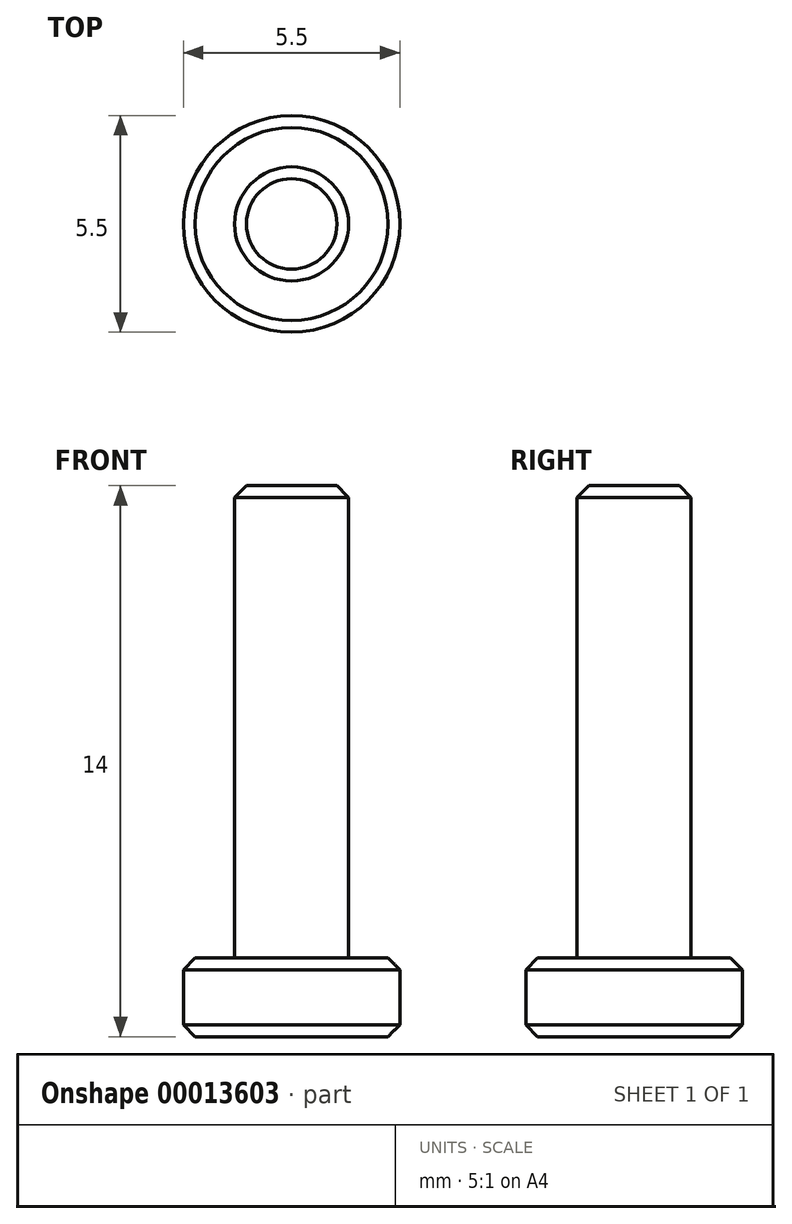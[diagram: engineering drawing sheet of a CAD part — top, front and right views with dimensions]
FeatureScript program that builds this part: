
annotation { "Feature Type Name" : "Feature", "Feature Type Description" : "" }
export const myFeature = defineFeature(function(context is Context, id is Id, definition is map)
    precondition{}
    {
        {
            var Q0;
            Q0=qCreatedBy(makeId("Top.planeOp"),FACE);
            var sketch = newSketch(context, id + "F0", { "sketchPlane" : qUnion([Q0])});
            skCircle(sketch, "E0", {"center": v(0, 0) * mm, "radius": 2.75 * mm});
            skCircle(sketch, "E1", {"center": v(0, 0) * mm, "radius": 1.45 * mm});
            skSolve(sketch);
        }
        {
            var Q0;
            Q0=makeQuery(id+"F0.imprint","IMPRINT",FACE,{"disambiguationData":[TD([[makeQuery(id+"F0.imprint","IMPRINT",EDGE,{"derivedFrom":sQuery(id+"F0.wireOp",EDGE,"E1")}),1.0]])]});
            var Q1;
            Q1=makeQuery(id+"F0.imprint","IMPRINT",FACE,{"disambiguationData":[TD([[makeQuery(id+"F0.imprint","IMPRINT",EDGE,{"derivedFrom":sQuery(id+"F0.wireOp",EDGE,"E0")}),1.0]])]});
            extrude(context, id + "F1", {"entities" : qUnion([Q0, Q1]), "oppositeDirection" : true, "depth" : 2 * mm});
        }
        {
            var Q0;
            Q0=makeQuery(id+"F0.imprint","IMPRINT",FACE,{"disambiguationData":[TD([[makeQuery(id+"F0.imprint","IMPRINT",EDGE,{"derivedFrom":sQuery(id+"F0.wireOp",EDGE,"E1")}),1.0]])]});
            extrude(context, id + "F2", {"entities" : qUnion([Q0]), "operationType" : NewBodyOperationType.ADD, "depth" : 12 * mm});
        }
        {
            var Q0;
            Q0=makeQuery(id+"F2.opExtrude","CAP_EDGE",EDGE,{"disambiguationData":[OSD([sQuery(id+"F0.wireOp",EDGE,"E1")])],"isStart":false});
            var Q1;
            Q1=makeQuery(id+"F1.opExtrude","CAP_EDGE",EDGE,{"disambiguationData":[OSD([sQuery(id+"F0.wireOp",EDGE,"E0")])],"isStart":true});
            var Q2;
            Q2=makeQuery(id+"F1.opExtrude","CAP_EDGE",EDGE,{"disambiguationData":[OSD([sQuery(id+"F0.wireOp",EDGE,"E0")])],"isStart":false});
            var Q3;
            Q3=makeQuery(id+"F2.opExtrude","CAP_EDGE",EDGE,{"disambiguationData":[OSD([sQuery(id+"F0.wireOp",EDGE,"E1")])],"isStart":true});
            chamfer(context, id + "F3", {"entities" : qUnion([Q0, Q1, Q2, Q3]), "width" : 0.3 * mm, "tangentPropagation" : true});
        }
    });
